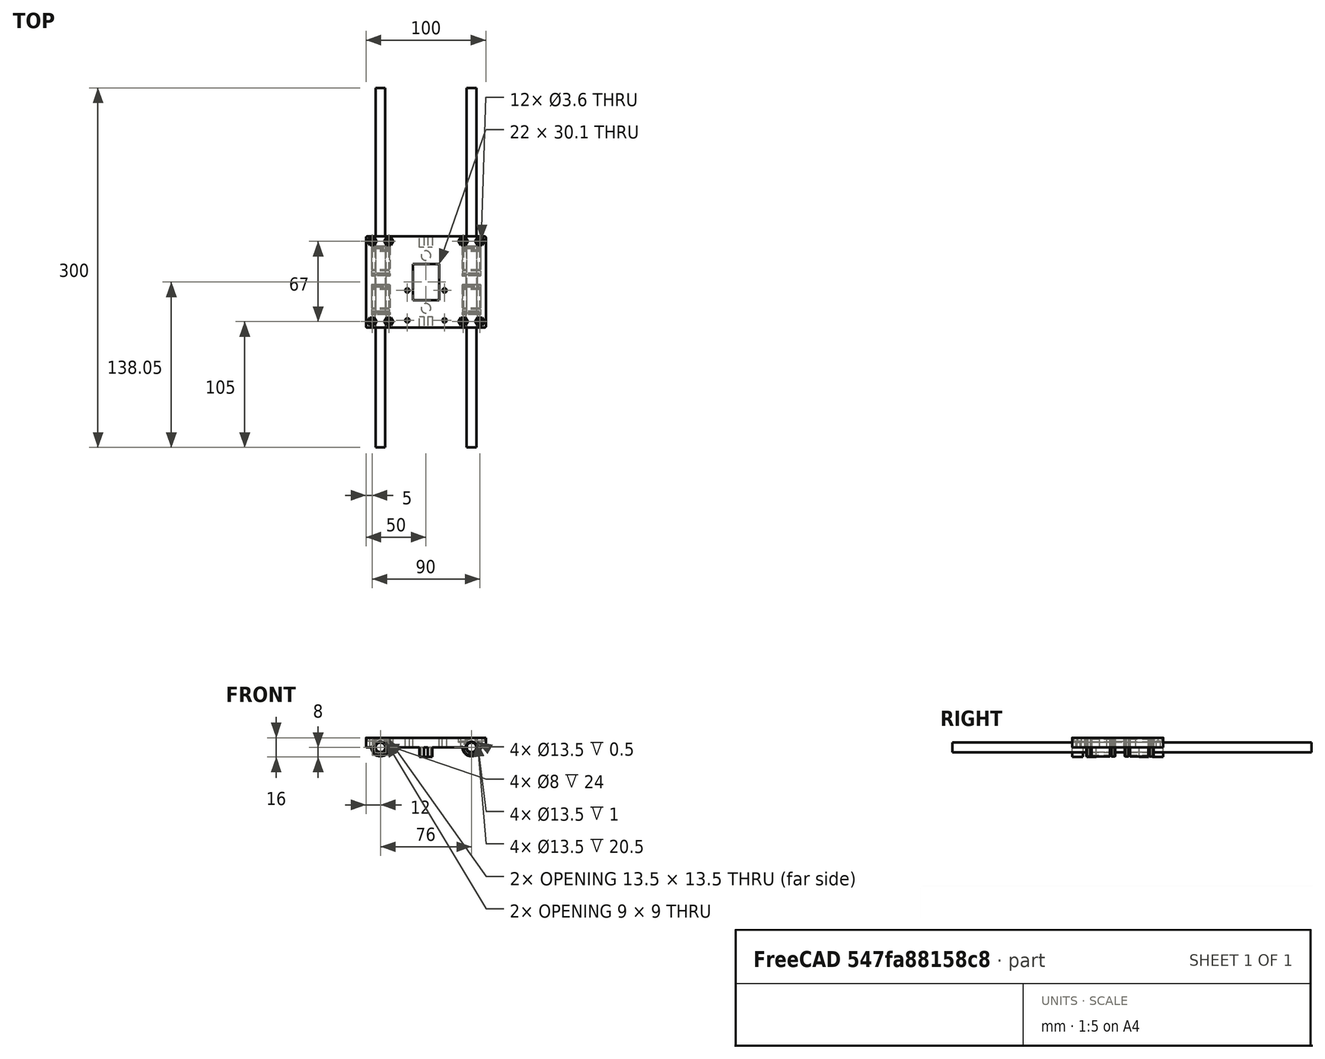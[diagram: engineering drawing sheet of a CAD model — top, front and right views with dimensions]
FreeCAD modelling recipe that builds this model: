
FCSTD DOCUMENT  (FreeCAD 0.18R4 (GitTag))
Label: rodamientos-soporte-ejes
License: All rights reserved
LicenseURL: http://en.wikipedia.org/wiki/All_rights_reserved
objects: Part::Cut×10, Part::Cylinder×8, Part::Feature×5, Part::Prism×4
note: 27 computed .brp shape members not serialized (recipe doc carries the construction recipe); baked Part::Feature solids carry a one-line shape summary decoded from their .brp

FEATURE [Part::Feature] Fillet003001  label="Soporte principal "
  shape: bbox 100 x 76.1 x 16 mm, 90 faces (baked)
FEATURE [Part::Cylinder] Cylinder037  label="Cilindro022"
  Angle = 360
  AttacherType = Attacher::AttachEngine3D
  Height = 20
  Placement = pos=(81,72,-10) rot=(0,0,1;0rad)
  Radius = 1.8
FEATURE [Part::Cut] Cut010035003015  label="Soporte principal'"
  Base = -> Fillet003001
  Tool = -> Cylinder037
FEATURE [Part::Prism] Prism004  label="Prisma004"
  AttacherType = Attacher::AttachEngine3D
  Circumradius = 3.7
  Height = 10
  Placement = pos=(81,72,5) rot=(0,0,1;0rad)
  Polygon = 6
FEATURE [Part::Cut] Cut010035003016  label="Soporte principal''"
  Base = -> Cut010035003015
  Tool = -> Prism004
FEATURE [Part::Cylinder] Cylinder039  label="Cilindro024"
  Angle = 360
  AttacherType = Attacher::AttachEngine3D
  Height = 20
  Placement = pos=(81,5,-10) rot=(0,0,1;0rad)
  Radius = 1.8
FEATURE [Part::Cut] Cut010035003019  label="Soporte principal ''''"
  Base = -> Cut010035003016
  Tool = -> Cylinder039
FEATURE [Part::Prism] Prism006  label="Prisma006"
  AttacherType = Attacher::AttachEngine3D
  Circumradius = 3.7
  Height = 10
  Placement = pos=(81,5,4) rot=(0,0,1;0rad)
  Polygon = 6
FEATURE [Part::Cut] Cut010035003021  label="Soporte principal V"
  Base = -> Cut010035003019
  Tool = -> Prism006
FEATURE [Part::Cylinder] Cylinder043  label="Cilindro028"
  Angle = 360
  AttacherType = Attacher::AttachEngine3D
  Height = 20
  Placement = pos=(19,72,-10) rot=(0,0,1;0rad)
  Radius = 1.8
FEATURE [Part::Cut] Cut010035003024  label="Soporte principal V'"
  Base = -> Cut010035003021
  Tool = -> Cylinder043
FEATURE [Part::Prism] Prism007  label="Prisma007"
  AttacherType = Attacher::AttachEngine3D
  Circumradius = 3.7
  Height = 10
  Placement = pos=(19,72,5) rot=(0,0,1;0rad)
  Polygon = 6
FEATURE [Part::Cut] Cut010035003025  label="Soporte principal V'''"
  Base = -> Cut010035003024
  Tool = -> Prism007
FEATURE [Part::Cylinder] Cylinder046  label="Cilindro031"
  Angle = 360
  AttacherType = Attacher::AttachEngine3D
  Height = 20
  Placement = pos=(19,5,-10) rot=(0,0,1;0rad)
  Radius = 1.8
FEATURE [Part::Cut] Cut010035003028  label="Soporte principal VI"
  Base = -> Cut010035003025
  Tool = -> Cylinder046
FEATURE [Part::Prism] Prism008  label="Prisma008"
  AttacherType = Attacher::AttachEngine3D
  Circumradius = 3.7
  Height = 10
  Placement = pos=(19,5,4) rot=(0,0,1;0rad)
  Polygon = 6
FEATURE [Part::Cut] Cut010035003029  label="Soporte principal VI'"
  Base = -> Cut010035003028
  Tool = -> Prism008
FEATURE [Part::Cylinder] Cylinder
  Angle = 360
  AttacherType = Attacher::AttachEngine3D
  Height = 100
  Placement = pos=(12,79,0) rot=(1,0,0;1.5708rad)
  Radius = 4.7
FEATURE [Part::Cylinder] Cylinder047
  Angle = 360
  AttacherType = Attacher::AttachEngine3D
  Height = 100
  Placement = pos=(88,79,0) rot=(1,0,0;1.5708rad)
  Radius = 4.7
FEATURE [Part::Cut] Cut
  Base = -> Cut010035003029
  Tool = -> Cylinder
FEATURE [Part::Cut] Cut010035003030
  Base = -> Cut
  Tool = -> Cylinder047
FEATURE [Part::Feature] Part__Feature  label="Lm8uu"
  Placement = pos=(12,24,0) rot=(1,0,0;1.5708rad)
  shape: bbox 15 x 24 x 15 mm, 26 faces (baked)
FEATURE [Part::Feature] Part__Feature001  label="Lm8uu001"
  Placement = pos=(88,24,0) rot=(1,0,0;1.5708rad)
  shape: bbox 15 x 24 x 15 mm, 26 faces (baked)
FEATURE [Part::Feature] Part__Feature002  label="Lm8uu002"
  Placement = pos=(88,56,0) rot=(1,0,0;1.5708rad)
  shape: bbox 15 x 24 x 15 mm, 26 faces (baked)
FEATURE [Part::Feature] Part__Feature003  label="Lm8uu003"
  Placement = pos=(12,56,0) rot=(1,0,0;1.5708rad)
  shape: bbox 15 x 24 x 15 mm, 26 faces (baked)
FEATURE [Part::Cylinder] Cylinder048  label="Eje1"
  Angle = 360
  AttacherType = Attacher::AttachEngine3D
  Height = 300
  Placement = pos=(88,200,0) rot=(1,0,0;1.5708rad)
  Radius = 4
FEATURE [Part::Cylinder] Cylinder049  label="Eje002"
  Angle = 360
  AttacherType = Attacher::AttachEngine3D
  Height = 300
  Placement = pos=(12,200,0) rot=(1,0,0;1.5708rad)
  Radius = 4
